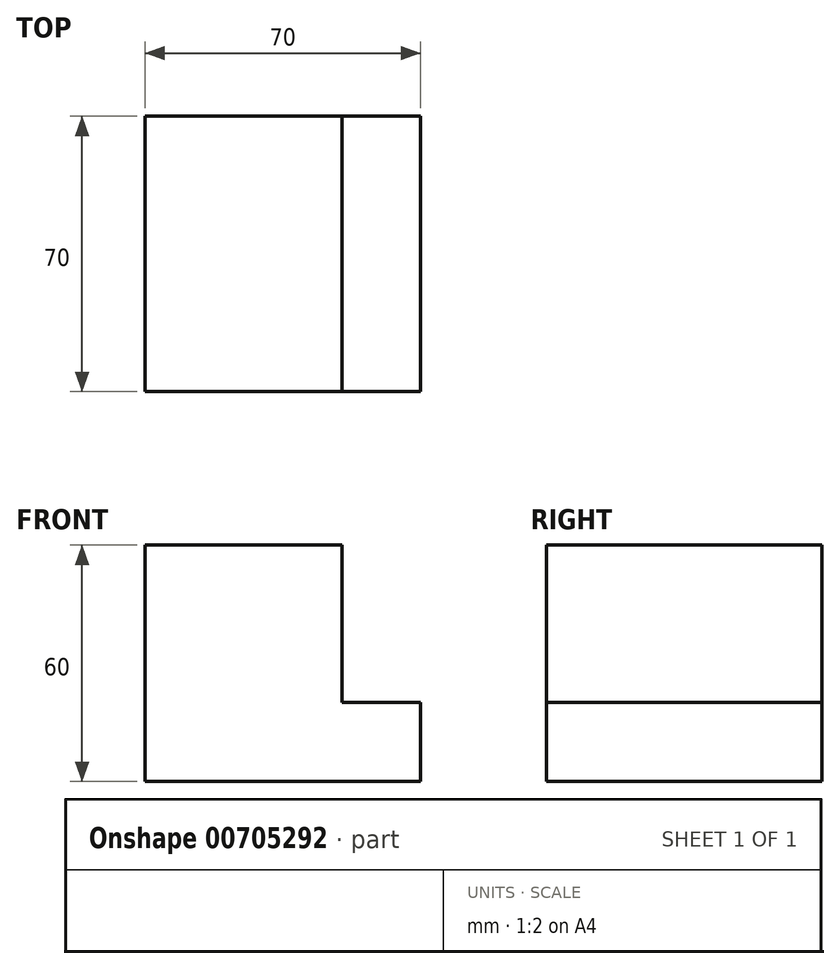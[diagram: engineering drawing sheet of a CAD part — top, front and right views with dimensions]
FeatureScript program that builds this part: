
annotation { "Feature Type Name" : "Feature", "Feature Type Description" : "" }
export const myFeature = defineFeature(function(context is Context, id is Id, definition is map)
    precondition{}
    {
        {
            var Q0;
            Q0=qCreatedBy(makeId("Front.planeOp"),FACE);
            var sketch = newSketch(context, id + "F0", { "sketchPlane" : qUnion([Q0])});
            skLineSegment(sketch, "E0.bottom", {"start": v(0, 0) * mm, "end": v(70, 0) * mm});
            skLineSegment(sketch, "E0.top", {"start": v(0, 60) * mm, "end": v(70, 60) * mm});
            skLineSegment(sketch, "E0.left", {"start": v(0, 0) * mm, "end": v(0, 60) * mm});
            skLineSegment(sketch, "E0.right", {"start": v(70, 0) * mm, "end": v(70, 60) * mm});
            skSolve(sketch);
        }
        {
            var Q0;
            Q0=makeQuery(id+"F0.imprint","IMPRINT",FACE,{"disambiguationData":[TD([[makeQuery(id+"F0.imprint","IMPRINT",EDGE,{"derivedFrom":sQuery(id+"F0.wireOp",EDGE,"E0.bottom")}),1.0]])]});
            extrude(context, id + "F1", {"entities" : qUnion([Q0]), "oppositeDirection" : true, "depth" : 70 * mm, "offsetDistance" : 25 * mm});
        }
        {
            var Q0;
            Q0=makeQuery(id+"F1.opExtrude","CAP_FACE",FACE,{"disambiguationData":[OSD([sQuery(id+"F0.wireOp",EDGE,"E0.bottom"),sQuery(id+"F0.wireOp",EDGE,"E0.top"),sQuery(id+"F0.wireOp",EDGE,"E0.left"),sQuery(id+"F0.wireOp",EDGE,"E0.right")])],"isStart":true});
            var sketch = newSketch(context, id + "F2", { "sketchPlane" : qUnion([Q0])});
            skLineSegment(sketch, "E1.bottom", {"start": v(50, 60) * mm, "end": v(70, 60) * mm});
            skLineSegment(sketch, "E1.top", {"start": v(50, 20) * mm, "end": v(70, 20) * mm});
            skLineSegment(sketch, "E1.left", {"start": v(50, 60) * mm, "end": v(50, 20) * mm});
            skLineSegment(sketch, "E1.right", {"start": v(70, 60) * mm, "end": v(70, 20) * mm});
            skSolve(sketch);
        }
        {
            var Q0;
            Q0=makeQuery(id+"F2.imprint","IMPRINT",FACE,{"disambiguationData":[TD([[makeQuery(id+"F2.imprint","IMPRINT",EDGE,{"derivedFrom":sQuery(id+"F2.wireOp",EDGE,"E1.bottom")}),-1.0]])]});
            extrude(context, id + "F3", {"entities" : qUnion([Q0]), "operationType" : NewBodyOperationType.REMOVE, "endBound" : BoundingType.THROUGH_ALL, "oppositeDirection" : true, "depth" : 25 * mm, "offsetDistance" : 25 * mm});
        }
    });
